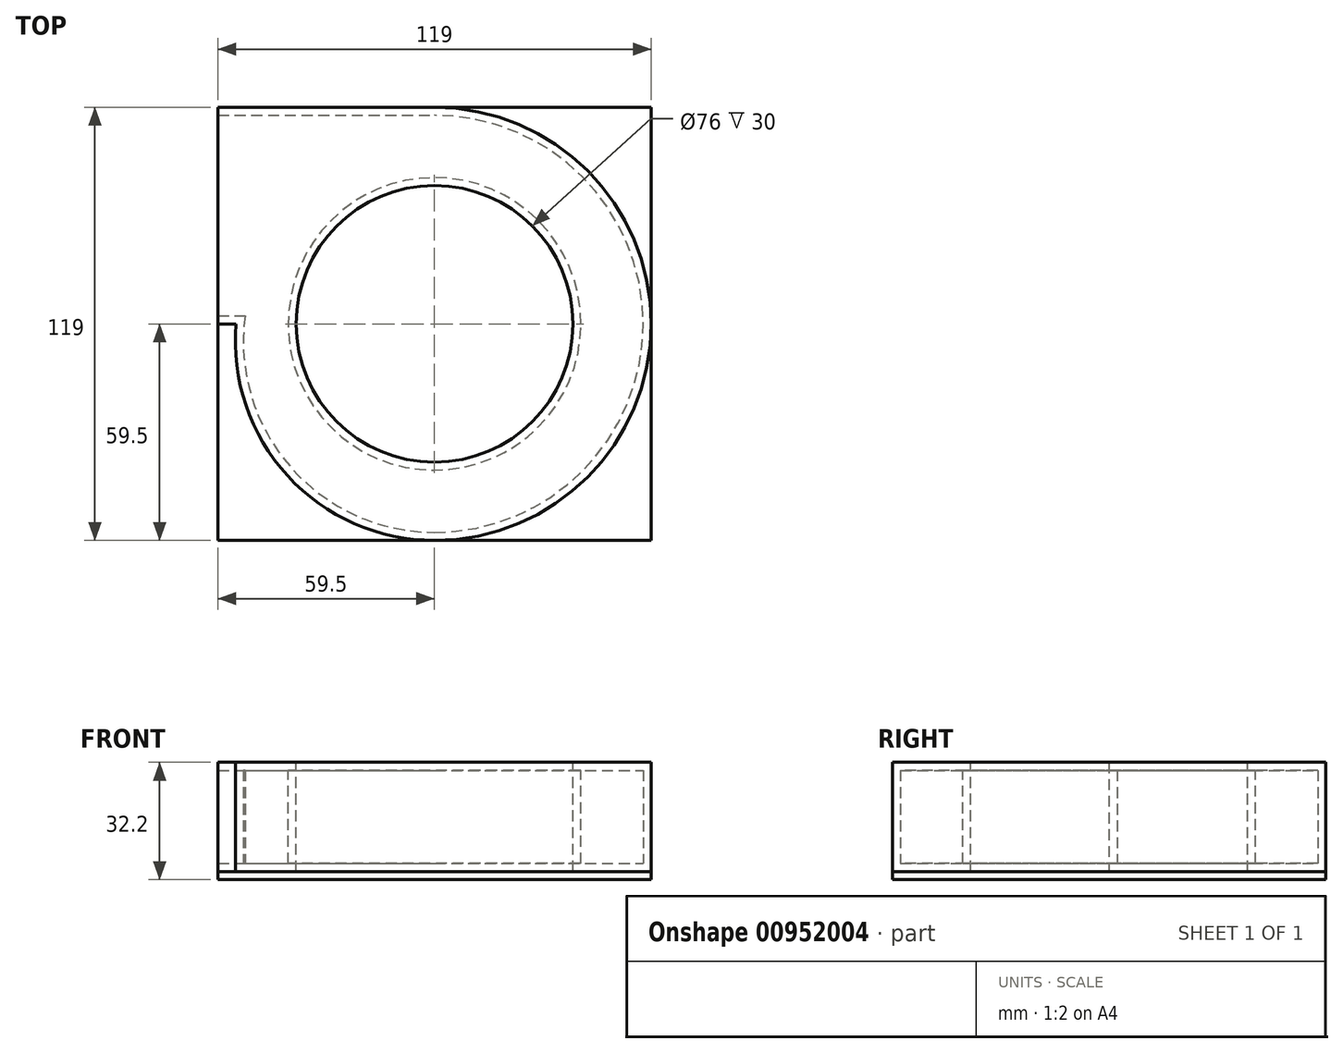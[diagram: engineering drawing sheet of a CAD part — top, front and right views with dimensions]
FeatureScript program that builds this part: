
annotation { "Feature Type Name" : "Feature", "Feature Type Description" : "" }
export const myFeature = defineFeature(function(context is Context, id is Id, definition is map)
    precondition{}
    {
        {
            var Q0;
            Q0=qCreatedBy(makeId("Top.planeOp"),FACE);
            var sketch = newSketch(context, id + "F0", { "sketchPlane" : qUnion([Q0])});
            skLineSegment(sketch, "E0.bottom", {"start": v(-59.5, 59.5) * mm, "end": v(59.5, 59.5) * mm});
            skLineSegment(sketch, "E0.top", {"start": v(-59.5, -59.5) * mm, "end": v(59.5, -59.5) * mm});
            skLineSegment(sketch, "E0.left", {"start": v(-59.5, 59.5) * mm, "end": v(-59.5, -59.5) * mm});
            skLineSegment(sketch, "E0.right", {"start": v(59.5, 59.5) * mm, "end": v(59.5, -59.5) * mm});
            skPoint(sketch, "E0.middle", {"position": v(0, 0) * mm});
            skSolve(sketch);
        }
        {
            var Q0;
            Q0 = qSketchRegion(id + "F0", true);
            extrude(context, id + "F1", {"entities" : qUnion([Q0]), "depth" : 2.2 * mm, "offsetDistance" : 25 * mm});
        }
        {
            var Q0;
            Q0=makeQuery(id+"F1.opExtrude","CAP_FACE",FACE,{"disambiguationData":[OSD([sQuery(id+"F0.wireOp",EDGE,"E0.bottom"),sQuery(id+"F0.wireOp",EDGE,"E0.top"),sQuery(id+"F0.wireOp",EDGE,"E0.left"),sQuery(id+"F0.wireOp",EDGE,"E0.right")])],"isStart":false});
            var sketch = newSketch(context, id + "F2", { "sketchPlane" : qUnion([Q0])});
            skArc(sketch, "E1", {"start": v(0, -59.5) * mm, "mid": v(59.5, 0) * mm, "end": v(0, 59.5) * mm});
            skLineSegment(sketch, "E2", {"start": v(0, 59.5) * mm, "end": v(0, -59.5) * mm, "construction": true});
            skLineSegment(sketch, "E3", {"start": v(0, 59.5) * mm, "end": v(-59.5, 59.5) * mm});
            skLineSegment(sketch, "E4", {"start": v(-59.5, 59.5) * mm, "end": v(-59.5, 0) * mm});
            skLineSegment(sketch, "E5", {"start": v(-59.5, 0) * mm, "end": v(-54.5, 0) * mm});
            skArc(sketch, "E6", {"start": v(0, -59.5) * mm, "mid": v(-40.34, -41.74) * mm, "end": v(-54.5, 0) * mm});
            skSolve(sketch);
        }
        {
            var Q0;
            Q0 = qSketchRegion(id + "F2", true);
            extrude(context, id + "F3", {"entities" : qUnion([Q0]), "depth" : 30 * mm, "offsetDistance" : 25 * mm});
        }
        {
            var Q0;
            Q0=makeQuery(id+"F3.opExtrude","CAP_FACE",FACE,{"disambiguationData":[OSD([sQuery(id+"F2.wireOp",EDGE,"E1"),sQuery(id+"F2.wireOp",EDGE,"E3"),sQuery(id+"F2.wireOp",EDGE,"E4"),sQuery(id+"F2.wireOp",EDGE,"E5"),sQuery(id+"F2.wireOp",EDGE,"E6")])],"isStart":false});
            var sketch = newSketch(context, id + "F4", { "sketchPlane" : qUnion([Q0])});
            skCircle(sketch, "E7", {"center": v(0, 0) * mm, "radius": 38 * mm});
            skSolve(sketch);
        }
        {
            var Q0;
            Q0 = qSketchRegion(id + "F4", true);
            var Q1;
            Q1=makeQuery(id+"F3.opExtrude","CAP_FACE",FACE,{"disambiguationData":[OSD([sQuery(id+"F2.wireOp",EDGE,"E1"),sQuery(id+"F2.wireOp",EDGE,"E3"),sQuery(id+"F2.wireOp",EDGE,"E4"),sQuery(id+"F2.wireOp",EDGE,"E5"),sQuery(id+"F2.wireOp",EDGE,"E6")])],"isStart":true});
            extrude(context, id + "F5", {"entities" : qUnion([Q0]), "operationType" : NewBodyOperationType.REMOVE, "endBound" : BoundingType.UP_TO_NEXT, "oppositeDirection" : true, "depth" : 25 * mm, "endBoundEntityFace" : qUnion([Q1]), "offsetDistance" : 25 * mm});
        }
        {
            var Q0;
            Q0=makeQuery(id+"F3.opExtrude","SWEPT_FACE",FACE,{"disambiguationData":[OSD([sQuery(id+"F2.wireOp",EDGE,"E4")])]});
            shell(context, id + "F6", {"entities" : qUnion([Q0]), "thickness" : 2.2 * mm});
        }
        {
            var Q0;
            Q0=makeQuery(id+"F1.opExtrude","CAP_FACE",FACE,{"disambiguationData":[OSD([sQuery(id+"F0.wireOp",EDGE,"E0.bottom"),sQuery(id+"F0.wireOp",EDGE,"E0.top"),sQuery(id+"F0.wireOp",EDGE,"E0.left"),sQuery(id+"F0.wireOp",EDGE,"E0.right")])],"isStart":false});
            extrude(context, id + "F7", {"entities" : qUnion([Q0]), "operationType" : NewBodyOperationType.ADD, "oppositeDirection" : true, "depth" : 1 * mm, "offsetDistance" : 25 * mm});
        }
    });
